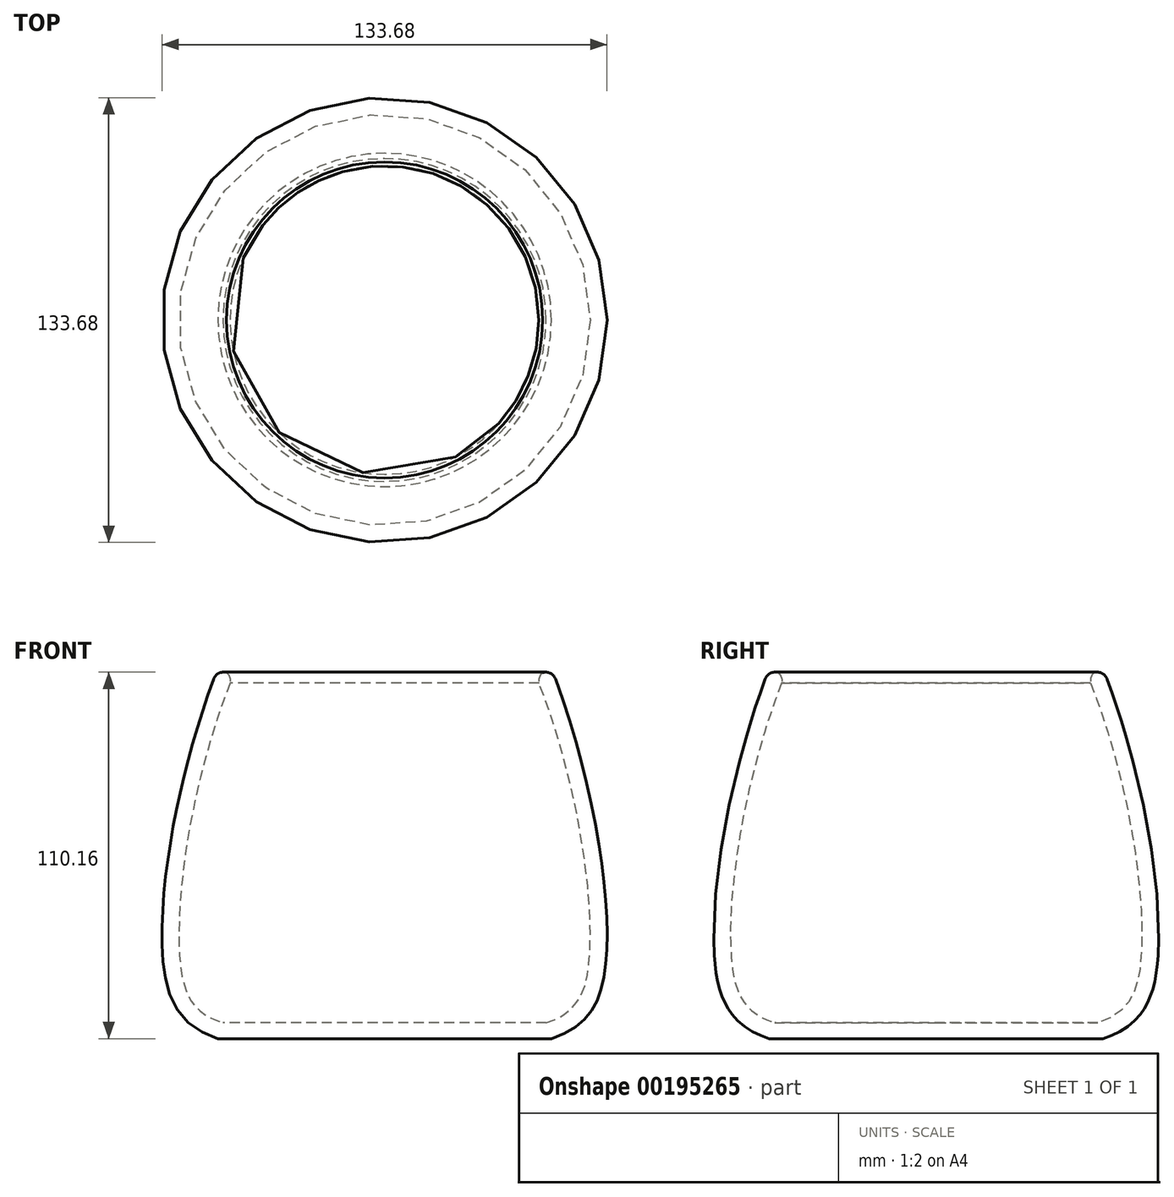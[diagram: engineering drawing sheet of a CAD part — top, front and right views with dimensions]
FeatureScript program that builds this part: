
annotation { "Feature Type Name" : "Feature", "Feature Type Description" : "" }
export const myFeature = defineFeature(function(context is Context, id is Id, definition is map)
    precondition{}
    {
        {
            var Q0;
            Q0=qCreatedBy(makeId("Front.planeOp"),FACE);
            var sketch = newSketch(context, id + "F0", { "sketchPlane" : qUnion([Q0])});
            skLineSegment(sketch, "E0", {"start": v(0, 0) * mm, "end": v(-50.09, 0) * mm});
            skFitSpline(sketch, "E1", {"points": [v(-50.09, 0) * mm, v(-66.7, 25.67) * mm, v(-50.09, 111.47) * mm], "startDerivative": vector(-101.44, 32.77) * mm, "endDerivative": vector(55.18, 144.87) * mm});
            skFitSpline(sketch, "E2.0", {"points": [v(-48.52, 4.83) * mm, v(-50.34, 5.42) * mm, v(-52.6, 6.43) * mm, v(-54.9, 7.97) * mm, v(-56.32, 9.22) * mm, v(-57.5, 10.6) * mm, v(-58.51, 12.13) * mm, v(-59.37, 13.86) * mm, v(-60.33, 16.5) * mm, v(-61.02, 19.63) * mm, v(-61.4, 22.81) * mm, v(-61.55, 24.75) * mm, v(-61.67, 26.78) * mm, v(-61.76, 29.43) * mm, v(-61.77, 33.91) * mm, v(-61.52, 39.94) * mm, v(-60.8, 47.73) * mm, v(-59.33, 58.73) * mm, v(-56.52, 73.38) * mm, v(-51.7, 91.63) * mm, v(-47.6, 103.74) * mm, v(-45.34, 109.66) * mm]});
            skLineSegment(sketch, "E3", {"start": v(-48.52, 4.83) * mm, "end": v(0, 4.83) * mm});
            skLineSegment(sketch, "E4", {"start": v(0, 4.83) * mm, "end": v(0, 0) * mm});
            skLineSegment(sketch, "E5", {"start": v(-48.03, 110.39) * mm, "end": v(-46.9, 109.8) * mm});
            skArc(sketch, "E6.filletArc", {"start": v(-46.9, 109.8) * mm, "mid": v(-49.52, 109.94) * mm, "end": v(-51.35, 108.07) * mm});
            skPoint(sketch, "E7.visualSharp", {"position": v(-45.55, 109.1) * mm});
            skArc(sketch, "E7.filletArc", {"start": v(-46.52, 106.49) * mm, "mid": v(-46.54, 108.72) * mm, "end": v(-48.03, 110.39) * mm});
            skSolve(sketch);
        }
        {
            var Q0;
            Q0=makeQuery(id+"F0.imprint","IMPRINT",FACE,{"disambiguationData":[TD([[makeQuery(id+"F0.imprint","IMPRINT",EDGE,{"derivedFrom":sQuery(id+"F0.wireOp",EDGE,"E0")}),-1.0]])]});
            var Q1;
            Q1=sQuery(id+"F0.wireOp",EDGE,"E4");
            revolve(context, id + "F1", {"entities" : qUnion([Q0]), "axis" : qUnion([Q1]), "revolveType" : RevolveType.FULL});
        }
    });
